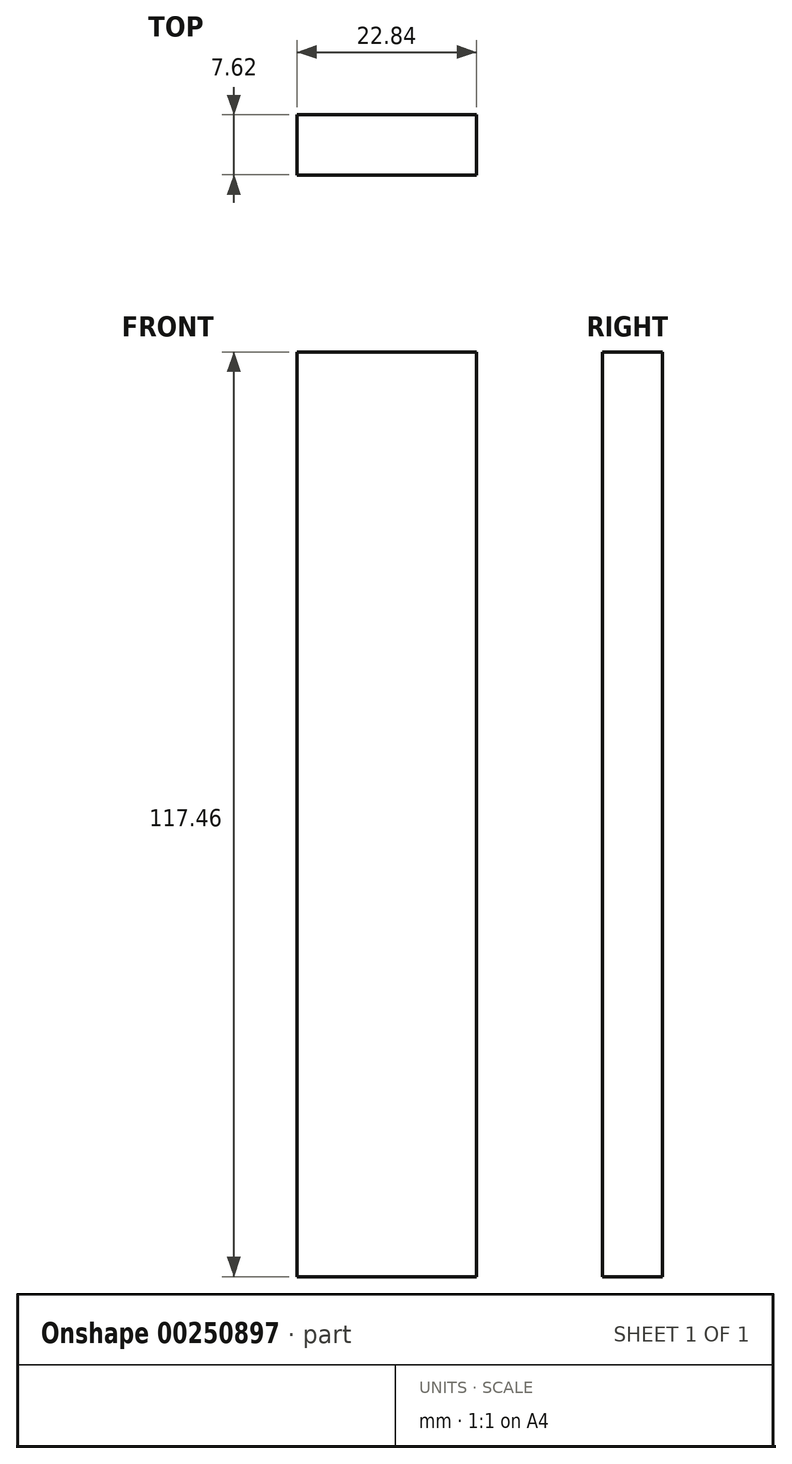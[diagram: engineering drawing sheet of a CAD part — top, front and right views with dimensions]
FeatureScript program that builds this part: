
annotation { "Feature Type Name" : "Feature", "Feature Type Description" : "" }
export const myFeature = defineFeature(function(context is Context, id is Id, definition is map)
    precondition{}
    {
        {
            var Q0;
            Q0=qCreatedBy(makeId("Front.planeOp"),FACE);
            var sketch = newSketch(context, id + "F0", { "sketchPlane" : qUnion([Q0])});
            skLineSegment(sketch, "E0.bottom", {"start": v(-11.42, -58.73) * mm, "end": v(11.43, -58.73) * mm});
            skLineSegment(sketch, "E0.top", {"start": v(-11.43, 58.73) * mm, "end": v(11.42, 58.73) * mm});
            skLineSegment(sketch, "E0.left", {"start": v(-11.42, -58.73) * mm, "end": v(-11.43, 58.73) * mm});
            skLineSegment(sketch, "E0.right", {"start": v(11.43, -58.73) * mm, "end": v(11.42, 58.73) * mm});
            skPoint(sketch, "E0.middle", {"position": v(0, 0) * mm});
            skSolve(sketch);
        }
        {
            var Q0;
            Q0=makeQuery(id+"F0.imprint","IMPRINT",FACE,{"disambiguationData":[TD([[makeQuery(id+"F0.imprint","IMPRINT",EDGE,{"derivedFrom":sQuery(id+"F0.wireOp",EDGE,"E0.bottom")}),1.0]])]});
            extrude(context, id + "F1", {"entities" : qUnion([Q0]), "endBound" : BoundingType.SYMMETRIC, "depth" : 7.63 * mm});
        }
    });
